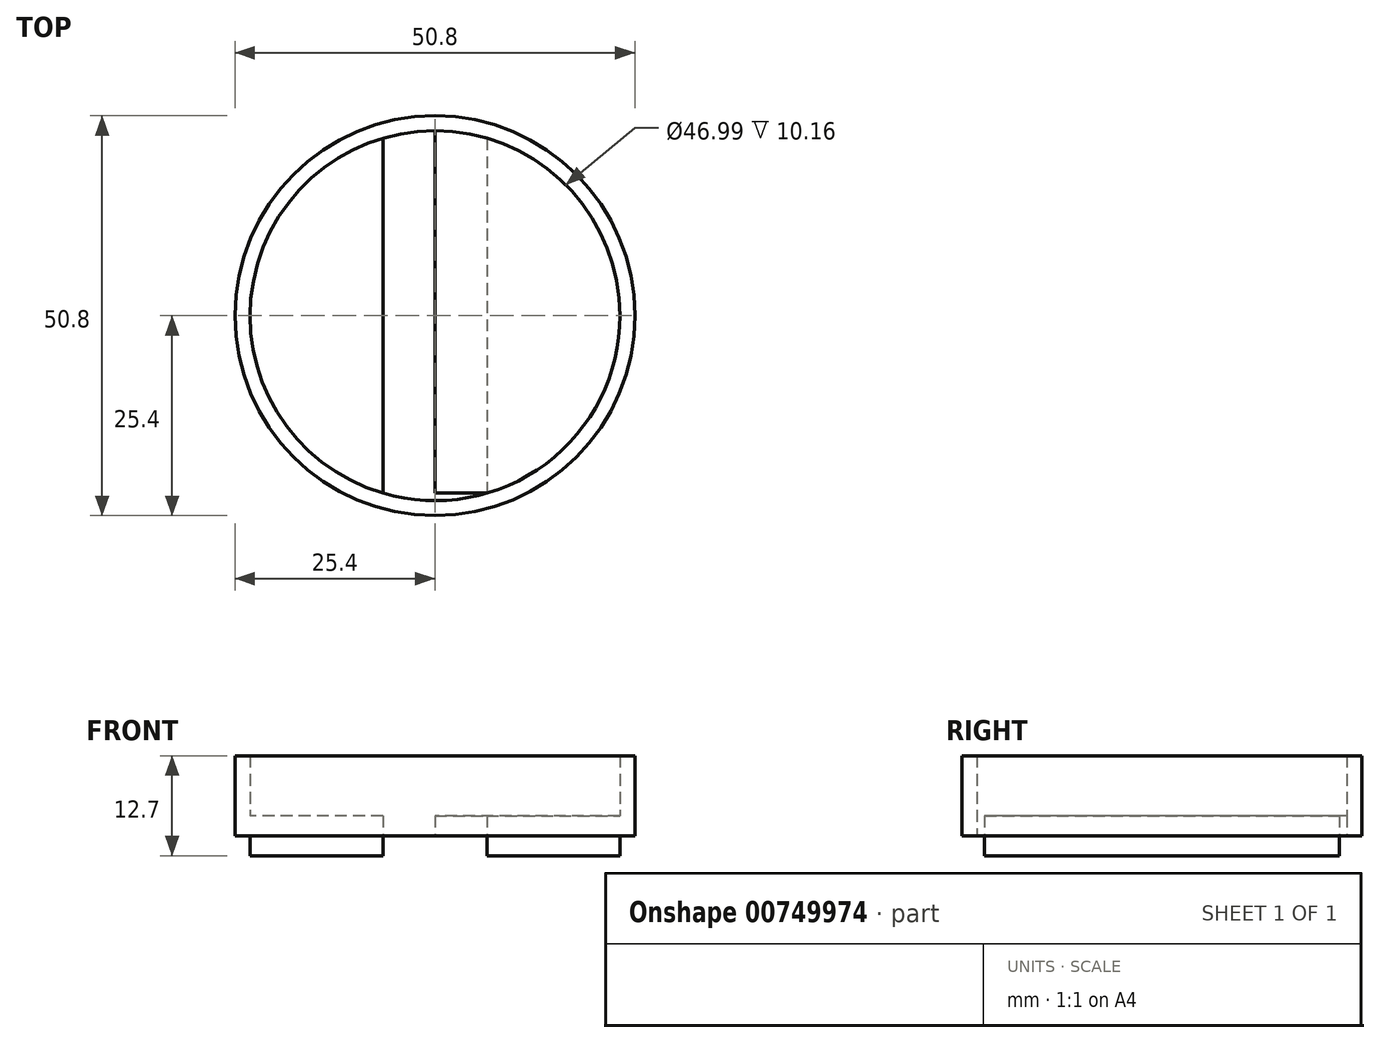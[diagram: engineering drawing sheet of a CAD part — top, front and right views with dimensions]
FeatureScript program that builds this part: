
annotation { "Feature Type Name" : "Feature", "Feature Type Description" : "" }
export const myFeature = defineFeature(function(context is Context, id is Id, definition is map)
    precondition{}
    {
        {
            var Q0;
            Q0=qCreatedBy(makeId("Top.planeOp"),FACE);
            var sketch = newSketch(context, id + "F0", { "sketchPlane" : qUnion([Q0])});
            skCircle(sketch, "E0", {"center": v(0, 0) * mm, "radius": 23.5 * mm});
            skCircle(sketch, "E1", {"center": v(0, 0) * mm, "radius": 25.4 * mm});
            skLineSegment(sketch, "E2", {"start": v(0, 23.5) * mm, "end": v(0, -23.5) * mm});
            skLineSegment(sketch, "E3.bottom", {"start": v(0, 23.5) * mm, "end": v(6.6, 23.5) * mm});
            skLineSegment(sketch, "E3.top", {"start": v(0, -22.55) * mm, "end": v(6.6, -22.55) * mm});
            skLineSegment(sketch, "E3.left", {"start": v(0, 23.5) * mm, "end": v(0, -22.55) * mm});
            skLineSegment(sketch, "E3.right", {"start": v(6.6, 23.5) * mm, "end": v(6.6, -22.55) * mm});
            skLineSegment(sketch, "E4.MirrorCS", {"start": v(-6.6, 23.5) * mm, "end": v(-6.6, -22.55) * mm});
            skLineSegment(sketch, "E5.MirrorCS", {"start": v(0, 23.5) * mm, "end": v(-6.6, 23.5) * mm});
            skLineSegment(sketch, "E6.MirrorCS", {"start": v(0, -22.55) * mm, "end": v(-6.6, -22.55) * mm});
            skSolve(sketch);
        }
        {
            var Q0;
            Q0=makeQuery(id+"F0.imprint","IMPRINT",FACE,{"disambiguationData":[TD([[makeQuery(id+"F0.imprint","IMPRINT",EDGE,{"derivedFrom":sQuery(id+"F0.wireOp",EDGE,"E1")}),1.0]])]});
            var Q1;
            {var subQ0=sQuery(id+"F0.wireOp",EDGE,"E5.MirrorCS");Q1=makeQuery(id+"F0.imprint","IMPRINT",FACE,{"disambiguationData":[TD([[makeQuery(id+"F0.imprint","IMPRINT",EDGE,{"derivedFrom":subQ0}),1.0]])]});}
            var Q2;
            {var subQ0=sQuery(id+"F0.wireOp",EDGE,"E3.bottom");Q2=makeQuery(id+"F0.imprint","IMPRINT",FACE,{"disambiguationData":[TD([[makeQuery(id+"F0.imprint","IMPRINT",EDGE,{"derivedFrom":subQ0}),-1.0]])]});}
            extrude(context, id + "F1", {"entities" : qUnion([Q0, Q1, Q2]), "depth" : 10.16 * mm, "offsetDistance" : 25.4 * mm});
        }
        {
            var Q0;
            {var subQ0=sQuery(id+"F0.wireOp",EDGE,"E4.MirrorCS");var subQ1=sQuery(id+"F0.wireOp",EDGE,"E0");var subQ3=makeQuery(id+"F0.imprint","INTERSECT",VERTEX,{"derivedFrom":[subQ1,subQ0]});Q0=makeQuery(id+"F0.imprint","IMPRINT",FACE,{"disambiguationData":[TD([[makeQuery(id+"F0.imprint","IMPRINT",EDGE,{"disambiguationData":[TD([[subQ3,-1.0]])],"derivedFrom":subQ1}),1.0]])]});}
            var Q1;
            {var subQ0=sQuery(id+"F0.wireOp",EDGE,"E3.left");Q1=makeQuery(id+"F0.imprint","IMPRINT",FACE,{"disambiguationData":[TD([[makeQuery(id+"F0.imprint","IMPRINT",EDGE,{"derivedFrom":subQ0}),-1.0]])]});}
            var Q2;
            {var subQ4=sQuery(id+"F0.wireOp",EDGE,"E3.top");Q2=makeQuery(id+"F0.imprint","IMPRINT",FACE,{"disambiguationData":[TD([[makeQuery(id+"F0.imprint","IMPRINT",EDGE,{"derivedFrom":subQ4}),1.0]])]});}
            var Q3;
            {var subQ0=sQuery(id+"F0.wireOp",EDGE,"E3.right");var subQ1=sQuery(id+"F0.wireOp",EDGE,"E0");var subQ3=makeQuery(id+"F0.imprint","INTERSECT",VERTEX,{"derivedFrom":[subQ1,subQ0]});Q3=makeQuery(id+"F0.imprint","IMPRINT",FACE,{"disambiguationData":[TD([[makeQuery(id+"F0.imprint","IMPRINT",EDGE,{"disambiguationData":[TD([[subQ3,1.0]])],"derivedFrom":subQ1}),1.0]])]});}
            extrude(context, id + "F2", {"entities" : qUnion([Q0, Q1, Q2, Q3]), "operationType" : NewBodyOperationType.ADD, "depth" : 2.54 * mm, "offsetDistance" : 25.4 * mm});
        }
        {
            var Q0;
            {var subQ0=sQuery(id+"F0.wireOp",EDGE,"E4.MirrorCS");var subQ1=sQuery(id+"F0.wireOp",EDGE,"E0");var subQ3=makeQuery(id+"F0.imprint","INTERSECT",VERTEX,{"derivedFrom":[subQ1,subQ0]});Q0=makeQuery(id+"F0.imprint","IMPRINT",FACE,{"disambiguationData":[TD([[makeQuery(id+"F0.imprint","IMPRINT",EDGE,{"disambiguationData":[TD([[subQ3,-1.0]])],"derivedFrom":subQ1}),1.0]])]});}
            var Q1;
            {var subQ0=sQuery(id+"F0.wireOp",EDGE,"E3.right");var subQ1=sQuery(id+"F0.wireOp",EDGE,"E0");var subQ3=makeQuery(id+"F0.imprint","INTERSECT",VERTEX,{"derivedFrom":[subQ1,subQ0]});Q1=makeQuery(id+"F0.imprint","IMPRINT",FACE,{"disambiguationData":[TD([[makeQuery(id+"F0.imprint","IMPRINT",EDGE,{"disambiguationData":[TD([[subQ3,1.0]])],"derivedFrom":subQ1}),1.0]])]});}
            extrude(context, id + "F3", {"entities" : qUnion([Q0, Q1]), "operationType" : NewBodyOperationType.ADD, "oppositeDirection" : true, "depth" : 2.54 * mm, "offsetDistance" : 25.4 * mm});
        }
    });
